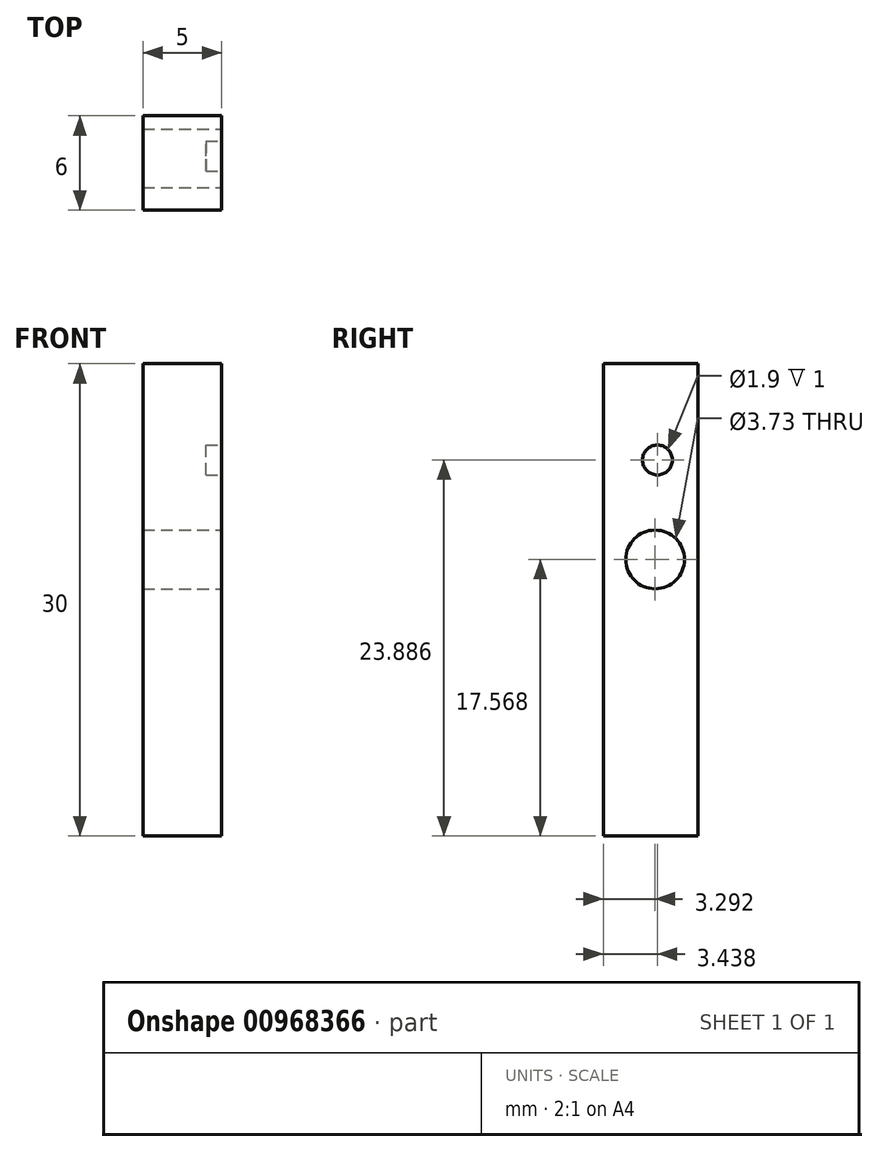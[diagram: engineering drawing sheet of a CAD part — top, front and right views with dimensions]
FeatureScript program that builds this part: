
annotation { "Feature Type Name" : "Feature", "Feature Type Description" : "" }
export const myFeature = defineFeature(function(context is Context, id is Id, definition is map)
    precondition{}
    {
        {
            var Q0;
            Q0=qCreatedBy(makeId("Front.planeOp"),FACE);
            var sketch = newSketch(context, id + "F0", { "sketchPlane" : qUnion([Q0])});
            skLineSegment(sketch, "E0.bottom", {"start": v(0, -15) * mm, "end": v(5, -15) * mm});
            skLineSegment(sketch, "E0.top", {"start": v(0, 15) * mm, "end": v(5, 15) * mm});
            skLineSegment(sketch, "E0.left", {"start": v(0, -15) * mm, "end": v(0, 15) * mm});
            skLineSegment(sketch, "E0.right", {"start": v(5, -15) * mm, "end": v(5, 15) * mm});
            skSolve(sketch);
        }
        {
            var Q0;
            Q0=makeQuery(id+"F0.imprint","IMPRINT",FACE,{"disambiguationData":[TD([[makeQuery(id+"F0.imprint","IMPRINT",EDGE,{"derivedFrom":sQuery(id+"F0.wireOp",EDGE,"E0.bottom")}),1.0]])]});
            extrude(context, id + "F1", {"entities" : qUnion([Q0]), "depth" : 6 * mm, "offsetDistance" : 25.4 * mm});
        }
        {
            var Q0;
            Q0=makeQuery(id+"F1.opExtrude","SWEPT_FACE",FACE,{"disambiguationData":[OSD([sQuery(id+"F0.wireOp",EDGE,"E0.right")])]});
            var sketch = newSketch(context, id + "F2", { "sketchPlane" : qUnion([Q0])});
            skCircle(sketch, "E1", {"center": v(-2.56, 8.89) * mm, "radius": 0.95 * mm});
            skSolve(sketch);
        }
        {
            var Q0;
            Q0 = qSketchRegion(id + "F2", true);
            extrude(context, id + "F3", {"entities" : qUnion([Q0]), "operationType" : NewBodyOperationType.REMOVE, "oppositeDirection" : true, "depth" : 1 * mm, "offsetDistance" : 25.4 * mm});
        }
        {
            var Q0;
            Q0=makeQuery(id+"F1.opExtrude","SWEPT_FACE",FACE,{"disambiguationData":[OSD([sQuery(id+"F0.wireOp",EDGE,"E0.right")])]});
            var sketch = newSketch(context, id + "F4", { "sketchPlane" : qUnion([Q0])});
            skCircle(sketch, "E2", {"center": v(-2.7, 2.57) * mm, "radius": 1.86 * mm});
            skSolve(sketch);
        }
        {
            var Q0;
            Q0 = qSketchRegion(id + "F4", true);
            extrude(context, id + "F5", {"entities" : qUnion([Q0]), "operationType" : NewBodyOperationType.REMOVE, "endBound" : BoundingType.THROUGH_ALL, "oppositeDirection" : true, "depth" : 25.4 * mm, "offsetDistance" : 25.4 * mm});
        }
    });
